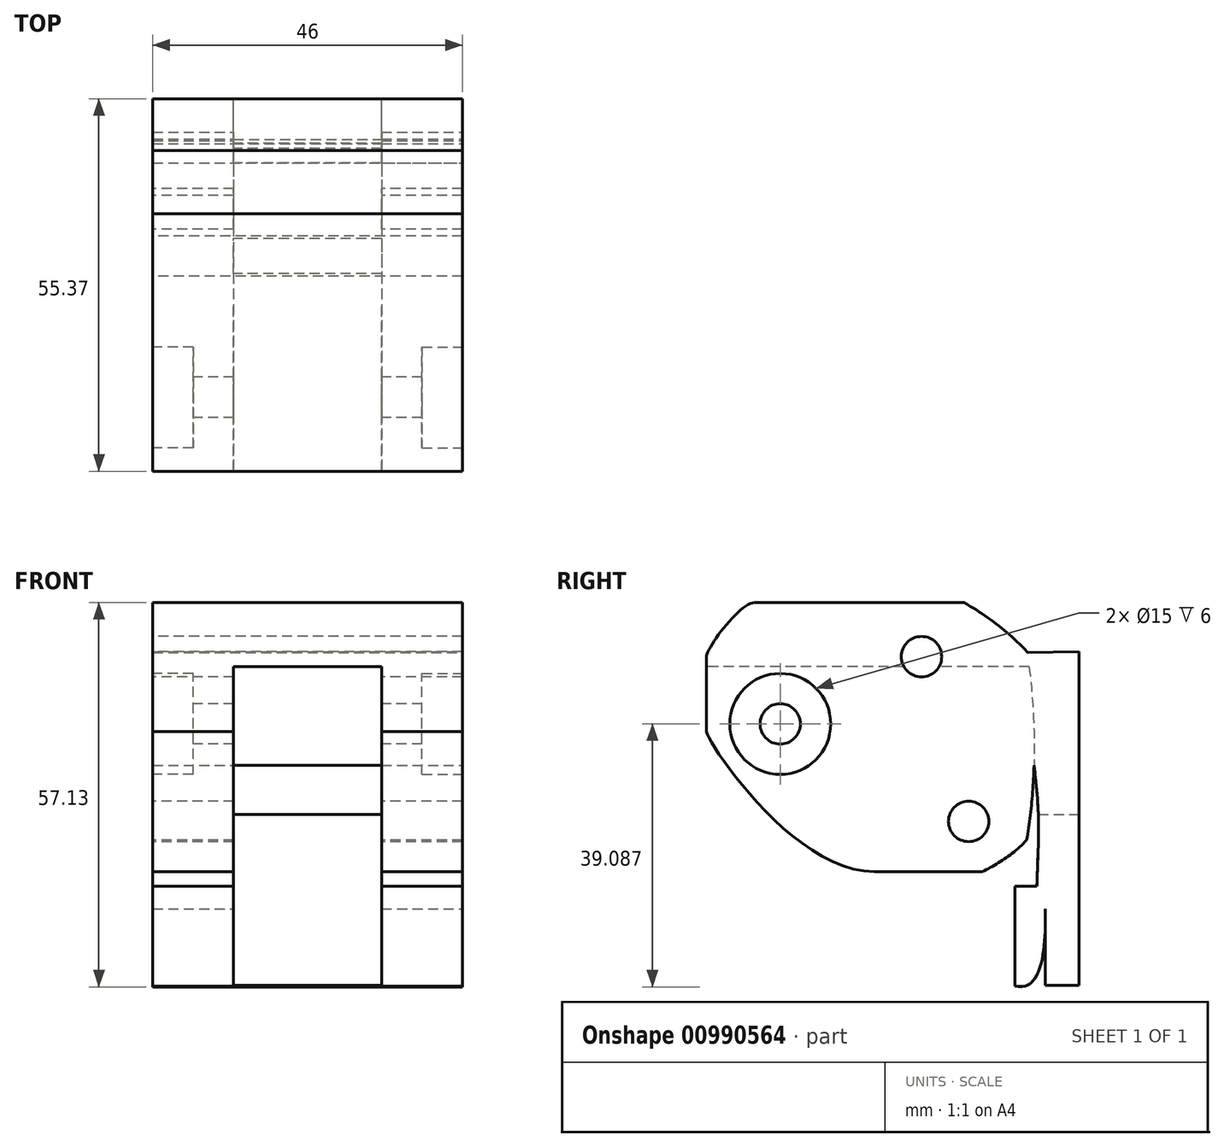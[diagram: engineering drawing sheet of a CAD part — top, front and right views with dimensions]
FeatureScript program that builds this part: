
annotation { "Feature Type Name" : "Feature", "Feature Type Description" : "" }
export const myFeature = defineFeature(function(context is Context, id is Id, definition is map)
    precondition{}
    {
        {
            var Q0;
            Q0=qCreatedBy(makeId("Right.planeOp"),FACE);
            var sketch = newSketch(context, id + "F0", { "sketchPlane" : qUnion([Q0])});
            skLineSegment(sketch, "E0", {"start": v(0, 0) * mm, "end": v(0, -40) * mm});
            skLineSegment(sketch, "E1", {"start": v(0, -40) * mm, "end": v(50, -40) * mm});
            skLineSegment(sketch, "E2", {"start": v(50, -40) * mm, "end": v(50, 0) * mm});
            skLineSegment(sketch, "E3", {"start": v(50, 0) * mm, "end": v(0, 0) * mm});
            skSolve(sketch);
        }
        {
            var Q0;
            Q0=makeQuery(id+"F0.imprint","IMPRINT",FACE,{"disambiguationData":[TD([[makeQuery(id+"F0.imprint","IMPRINT",EDGE,{"derivedFrom":sQuery(id+"F0.wireOp",EDGE,"E0")}),1.0]])]});
            extrude(context, id + "F1", {"entities" : qUnion([Q0]), "depth" : 46 * mm, "offsetDistance" : 25.4 * mm});
        }
        {
            var Q0;
            Q0=makeQuery(id+"F1.opExtrude","SWEPT_FACE",FACE,{"disambiguationData":[OSD([sQuery(id+"F0.wireOp",EDGE,"E0")])]});
            var sketch = newSketch(context, id + "F2", { "sketchPlane" : qUnion([Q0])});
            skLineSegment(sketch, "E4", {"start": v(0, -40) * mm, "end": v(12, -40) * mm});
            skLineSegment(sketch, "E5", {"start": v(12, -40) * mm, "end": v(12, -9.52) * mm});
            skLineSegment(sketch, "E6", {"start": v(12, -9.52) * mm, "end": v(34, -9.52) * mm});
            skLineSegment(sketch, "E7", {"start": v(34, -9.52) * mm, "end": v(34, -40) * mm});
            skLineSegment(sketch, "E8", {"start": v(34, -40) * mm, "end": v(46, -40) * mm});
            skLineSegment(sketch, "E9", {"start": v(12, -40) * mm, "end": v(34, -40) * mm});
            skSolve(sketch);
        }
        {
            var Q0;
            Q0=makeQuery(id+"F2.imprint","IMPRINT",FACE,{"disambiguationData":[TD([[makeQuery(id+"F2.imprint","IMPRINT",EDGE,{"derivedFrom":sQuery(id+"F2.wireOp",EDGE,"E5")}),-1.0]])]});
            extrude(context, id + "F3", {"entities" : qUnion([Q0]), "operationType" : NewBodyOperationType.REMOVE, "oppositeDirection" : true, "depth" : 50 * mm, "offsetDistance" : 25.4 * mm});
        }
        {
            var Q0;
            Q0=makeQuery(id+"F0.imprint","IMPRINT",FACE,{"disambiguationData":[TD([[makeQuery(id+"F0.imprint","IMPRINT",EDGE,{"derivedFrom":sQuery(id+"F0.wireOp",EDGE,"E0")}),1.0]])]});
            var sketch = newSketch(context, id + "F4", { "sketchPlane" : qUnion([Q0])});
            skCircle(sketch, "E10", {"center": v(11, -18.04) * mm, "radius": 3 * mm});
            skLineSegment(sketch, "E11", {"start": v(11, -18.04) * mm, "end": v(11, -40.04) * mm});
            skLineSegment(sketch, "E12", {"start": v(11, -18.04) * mm, "end": v(0, -18.04) * mm});
            skCircle(sketch, "E13", {"center": v(32, -8.04) * mm, "radius": 3 * mm});
            skLineSegment(sketch, "E14", {"start": v(11, -18.04) * mm, "end": v(32, -18.04) * mm});
            skLineSegment(sketch, "E15", {"start": v(32, -18.04) * mm, "end": v(32, -8.04) * mm});
            skCircle(sketch, "E16", {"center": v(39, -32.54) * mm, "radius": 3 * mm});
            skLineSegment(sketch, "E17", {"start": v(39, -32.54) * mm, "end": v(11, -32.54) * mm});
            skLineSegment(sketch, "E18", {"start": v(11, -32.54) * mm, "end": v(11, -18.04) * mm});
            skSolve(sketch);
        }
        {
            var Q0;
            {var subQ0=sQuery(id+"F4.wireOp",EDGE,"E14");var subQ1=sQuery(id+"F4.wireOp",EDGE,"E10");var subQ2=makeQuery(id+"F4.imprint","INTERSECT",VERTEX,{"derivedFrom":[subQ1,subQ0]});Q0=makeQuery(id+"F4.imprint","IMPRINT",FACE,{"disambiguationData":[TD([[makeQuery(id+"F4.imprint","IMPRINT",EDGE,{"disambiguationData":[TD([[subQ2,1.0]])],"derivedFrom":subQ1}),1.0]])]});}
            var Q1;
            {var subQ0=sQuery(id+"F4.wireOp",EDGE,"E12");var subQ1=sQuery(id+"F4.wireOp",EDGE,"E10");var subQ2=makeQuery(id+"F4.imprint","INTERSECT",VERTEX,{"derivedFrom":[subQ1,subQ0]});Q1=makeQuery(id+"F4.imprint","IMPRINT",FACE,{"disambiguationData":[TD([[makeQuery(id+"F4.imprint","IMPRINT",EDGE,{"disambiguationData":[TD([[subQ2,-1.0]])],"derivedFrom":subQ1}),1.0]])]});}
            var Q2;
            {var subQ0=sQuery(id+"F4.wireOp",EDGE,"E14");var subQ1=sQuery(id+"F4.wireOp",EDGE,"E10");var subQ2=makeQuery(id+"F4.imprint","INTERSECT",VERTEX,{"derivedFrom":[subQ1,subQ0]});Q2=makeQuery(id+"F4.imprint","IMPRINT",FACE,{"disambiguationData":[TD([[makeQuery(id+"F4.imprint","IMPRINT",EDGE,{"disambiguationData":[TD([[subQ2,-1.0]])],"derivedFrom":subQ1}),1.0]])]});}
            var Q3;
            Q3=sQuery(id+"F4.wireOp",EDGE,"E10");
            extrude(context, id + "F5", {"entities" : qUnion([Q0, Q1, Q2]), "operationType" : NewBodyOperationType.REMOVE, "surfaceEntities" : qUnion([Q3]), "depth" : 65 * mm, "offsetDistance" : 25.4 * mm});
        }
        {
            var Q0;
            Q0=makeQuery(id+"F4.imprint","IMPRINT",FACE,{"disambiguationData":[TD([[makeQuery(id+"F4.imprint","IMPRINT",EDGE,{"derivedFrom":sQuery(id+"F4.wireOp",EDGE,"E13")}),1.0]])]});
            extrude(context, id + "F6", {"entities" : qUnion([Q0]), "operationType" : NewBodyOperationType.REMOVE, "depth" : 65 * mm, "offsetDistance" : 25.4 * mm});
        }
        {
            var Q0;
            Q0=makeQuery(id+"F4.imprint","IMPRINT",FACE,{"disambiguationData":[TD([[makeQuery(id+"F4.imprint","IMPRINT",EDGE,{"derivedFrom":sQuery(id+"F4.wireOp",EDGE,"E16")}),1.0]])]});
            extrude(context, id + "F7", {"entities" : qUnion([Q0]), "operationType" : NewBodyOperationType.REMOVE, "depth" : 65 * mm, "offsetDistance" : 25.4 * mm});
        }
        {
            var Q0;
            Q0=makeQuery(id+"F0.imprint","IMPRINT",FACE,{"disambiguationData":[TD([[makeQuery(id+"F0.imprint","IMPRINT",EDGE,{"derivedFrom":sQuery(id+"F0.wireOp",EDGE,"E0")}),1.0]])]});
            var sketch = newSketch(context, id + "F8", { "sketchPlane" : qUnion([Q0])});
            skCircle(sketch, "E19", {"center": v(11, -18.04) * mm, "radius": 7.5 * mm});
            skSolve(sketch);
        }
        {
            var Q0;
            Q0=makeQuery(id+"F8.imprint","IMPRINT",FACE,{"disambiguationData":[TD([[makeQuery(id+"F8.imprint","IMPRINT",EDGE,{"derivedFrom":sQuery(id+"F8.wireOp",EDGE,"E19")}),1.0]])]});
            var Q1;
            Q1=sQuery(id+"F8.wireOp",EDGE,"E19");
            extrude(context, id + "F9", {"entities" : qUnion([Q0]), "operationType" : NewBodyOperationType.REMOVE, "surfaceEntities" : qUnion([Q1]), "depth" : 6 * mm, "offsetDistance" : 25.4 * mm});
        }
        {
            var Q0;
            Q0=makeQuery(id+"F1.opExtrude","CAP_FACE",FACE,{"disambiguationData":[OSD([sQuery(id+"F0.wireOp",EDGE,"E0"),sQuery(id+"F0.wireOp",EDGE,"E1"),sQuery(id+"F0.wireOp",EDGE,"E2"),sQuery(id+"F0.wireOp",EDGE,"E3")])],"isStart":false});
            var sketch = newSketch(context, id + "F10", { "sketchPlane" : qUnion([Q0])});
            skCircle(sketch, "E20", {"center": v(11, -18.04) * mm, "radius": 7.5 * mm});
            skSolve(sketch);
        }
        {
            var Q0;
            Q0=makeQuery(id+"F10.imprint","IMPRINT",FACE,{"disambiguationData":[TD([[makeQuery(id+"F10.imprint","IMPRINT",EDGE,{"derivedFrom":sQuery(id+"F10.wireOp",EDGE,"E20")}),1.0]])]});
            extrude(context, id + "F11", {"entities" : qUnion([Q0]), "operationType" : NewBodyOperationType.REMOVE, "oppositeDirection" : true, "depth" : 6 * mm, "offsetDistance" : 25.4 * mm});
        }
        {
            var Q0;
            Q0=makeQuery(id+"F1.opExtrude","CAP_FACE",FACE,{"disambiguationData":[OSD([sQuery(id+"F0.wireOp",EDGE,"E0"),sQuery(id+"F0.wireOp",EDGE,"E1"),sQuery(id+"F0.wireOp",EDGE,"E2"),sQuery(id+"F0.wireOp",EDGE,"E3")])],"isStart":false});
            var sketch = newSketch(context, id + "F12", { "sketchPlane" : qUnion([Q0])});
            skLineSegment(sketch, "E21", {"start": v(0, -19.17) * mm, "end": v(0, -40) * mm});
            skLineSegment(sketch, "E22", {"start": v(0, -40) * mm, "end": v(25, -40) * mm});
            skFitSpline(sketch, "E23", {"points": [v(0, -19.17) * mm, v(25, -40) * mm], "startDerivative": vector(1.52, -6.15) * mm, "endDerivative": vector(36.1, 0) * mm});
            skSolve(sketch);
        }
        {
            var Q0;
            Q0=makeQuery(id+"F12.imprint","IMPRINT",FACE,{"disambiguationData":[TD([[makeQuery(id+"F12.imprint","IMPRINT",EDGE,{"derivedFrom":sQuery(id+"F12.wireOp",EDGE,"E22")}),1.0]])]});
            extrude(context, id + "F13", {"entities" : qUnion([Q0]), "operationType" : NewBodyOperationType.REMOVE, "oppositeDirection" : true, "depth" : 66 * mm, "offsetDistance" : 25.4 * mm});
        }
        {
            var Q0;
            Q0=makeQuery(id+"F1.opExtrude","CAP_FACE",FACE,{"disambiguationData":[OSD([sQuery(id+"F0.wireOp",EDGE,"E0"),sQuery(id+"F0.wireOp",EDGE,"E1"),sQuery(id+"F0.wireOp",EDGE,"E2"),sQuery(id+"F0.wireOp",EDGE,"E3")])],"isStart":false});
            var sketch = newSketch(context, id + "F14", { "sketchPlane" : qUnion([Q0])});
            skLineSegment(sketch, "E24", {"start": v(7.17, 0) * mm, "end": v(0, 0) * mm});
            skLineSegment(sketch, "E25", {"start": v(0, 0) * mm, "end": v(0, -8.13) * mm});
            skFitSpline(sketch, "E26", {"points": [v(7.17, 0) * mm, v(0, -8.13) * mm], "startDerivative": vector(-6.42, 0) * mm, "endDerivative": vector(0, -4.06) * mm});
            skSolve(sketch);
        }
        {
            var Q0;
            Q0=makeQuery(id+"F14.imprint","IMPRINT",FACE,{"disambiguationData":[TD([[makeQuery(id+"F14.imprint","IMPRINT",EDGE,{"derivedFrom":sQuery(id+"F14.wireOp",EDGE,"E24")}),1.0]])]});
            extrude(context, id + "F15", {"entities" : qUnion([Q0]), "operationType" : NewBodyOperationType.REMOVE, "oppositeDirection" : true, "depth" : 100 * mm, "offsetDistance" : 25.4 * mm});
        }
        {
            var Q0;
            Q0=qCreatedBy(makeId("Right.planeOp"),FACE);
            var sketch = newSketch(context, id + "F16", { "sketchPlane" : qUnion([Q0])});
            skFitSpline(sketch, "E27", {"points": [v(38.3, 0) * mm, v(50.02, -10.07) * mm], "startDerivative": vector(13.92, -8.11) * mm, "endDerivative": vector(10.16, -13.26) * mm});
            skFitSpline(sketch, "E28", {"points": [v(50.05, -32.16) * mm, v(40.93, -40.02) * mm], "startDerivative": vector(-7.3, -11.71) * mm, "endDerivative": vector(-10.38, -4.86) * mm});
            skLineSegment(sketch, "E29", {"start": v(38.3, 0) * mm, "end": v(50.02, 0) * mm});
            skLineSegment(sketch, "E30", {"start": v(50.02, 0) * mm, "end": v(50.02, -10.07) * mm});
            skLineSegment(sketch, "E31", {"start": v(50.05, -32.16) * mm, "end": v(50.05, -40.06) * mm});
            skLineSegment(sketch, "E32", {"start": v(50.05, -40.06) * mm, "end": v(40.93, -40.02) * mm});
            skFitSpline(sketch, "E33", {"points": [v(47.68, -7.3) * mm, v(47.62, -35.32) * mm], "startDerivative": vector(4.14, -27.6) * mm, "endDerivative": vector(-4.56, -25.44) * mm});
            skLineSegment(sketch, "E34", {"start": v(47.68, -7.3) * mm, "end": v(50.02, -10.07) * mm});
            skLineSegment(sketch, "E35", {"start": v(50.05, -32.16) * mm, "end": v(47.62, -35.32) * mm});
            skLineSegment(sketch, "E36", {"start": v(50.02, -10.07) * mm, "end": v(50.05, -32.16) * mm});
            skSolve(sketch);
        }
        {
            var Q0;
            Q0 = qSketchRegion(id + "F16", true);
            extrude(context, id + "F17", {"entities" : qUnion([Q0]), "operationType" : NewBodyOperationType.REMOVE, "depth" : 254 * mm, "offsetDistance" : 25.4 * mm});
        }
        {
            var Q0;
            Q0=makeQuery(id+"F1.opExtrude","CAP_FACE",FACE,{"disambiguationData":[OSD([sQuery(id+"F0.wireOp",EDGE,"E0"),sQuery(id+"F0.wireOp",EDGE,"E1"),sQuery(id+"F0.wireOp",EDGE,"E2"),sQuery(id+"F0.wireOp",EDGE,"E3")])],"isStart":false});
            var sketch = newSketch(context, id + "F18", { "sketchPlane" : qUnion([Q0])});
            skLineSegment(sketch, "E37", {"start": v(55.37, -7.33) * mm, "end": v(55.37, -56.91) * mm});
            skLineSegment(sketch, "E38", {"start": v(49.14, -42.18) * mm, "end": v(45.85, -42.18) * mm});
            skLineSegment(sketch, "E39", {"start": v(45.85, -42.18) * mm, "end": v(45.85, -57.04) * mm});
            skLineSegment(sketch, "E40", {"start": v(45.84, -7.44) * mm, "end": v(55.37, -7.33) * mm});
            skFitSpline(sketch, "E41", {"points": [v(45.84, -7.44) * mm, v(49.14, -42.18) * mm], "startDerivative": vector(13.58, -69.76) * mm, "endDerivative": vector(-0.71, -29.2) * mm});
            skLineSegment(sketch, "E42", {"start": v(55.37, -56.91) * mm, "end": v(50.4, -56.91) * mm});
            skLineSegment(sketch, "E43", {"start": v(50.4, -56.91) * mm, "end": v(50.4, -45.54) * mm});
            skFitSpline(sketch, "E44", {"points": [v(50.4, -45.54) * mm, v(45.85, -57.04) * mm], "startDerivative": vector(0, -13.77) * mm, "endDerivative": vector(-13.68, 3.06) * mm});
            skSolve(sketch);
        }
        {
            var Q0;
            {var subQ1=sQuery(id+"F18.wireOp",EDGE,"E37");Q0=makeQuery(id+"F18.imprint","IMPRINT",FACE,{"disambiguationData":[TD([[makeQuery(id+"F18.imprint","IMPRINT",EDGE,{"derivedFrom":subQ1}),-1.0]])]});}
            extrude(context, id + "F19", {"entities" : qUnion([Q0]), "operationType" : NewBodyOperationType.ADD, "oppositeDirection" : true, "depth" : 46 * mm, "offsetDistance" : 25.4 * mm});
        }
        {
            var Q0;
            Q0=makeQuery(id+"F19.opExtrude","SWEPT_FACE",FACE,{"disambiguationData":[OSD([sQuery(id+"F18.wireOp",EDGE,"E37")])]});
            var sketch = newSketch(context, id + "F20", { "sketchPlane" : qUnion([Q0])});
            skLineSegment(sketch, "E45", {"start": v(-34, -56.91) * mm, "end": v(-34, -31.51) * mm});
            skLineSegment(sketch, "E46", {"start": v(-34, -31.51) * mm, "end": v(-12, -31.51) * mm});
            skLineSegment(sketch, "E47", {"start": v(-12, -31.51) * mm, "end": v(-12, -56.91) * mm});
            skLineSegment(sketch, "E48", {"start": v(-34, -56.91) * mm, "end": v(-12, -56.91) * mm});
            skLineSegment(sketch, "E49", {"start": v(-46, -56.91) * mm, "end": v(-34, -56.91) * mm});
            skLineSegment(sketch, "E50", {"start": v(-12, -56.91) * mm, "end": v(0, -56.91) * mm});
            skSolve(sketch);
        }
        {
            var Q0;
            Q0=makeQuery(id+"F20.imprint","IMPRINT",FACE,{"disambiguationData":[TD([[makeQuery(id+"F20.imprint","IMPRINT",EDGE,{"derivedFrom":sQuery(id+"F20.wireOp",EDGE,"E45")}),-1.0]])]});
            extrude(context, id + "F21", {"entities" : qUnion([Q0]), "operationType" : NewBodyOperationType.REMOVE, "oppositeDirection" : true, "depth" : 25.4 * mm, "offsetDistance" : 25.4 * mm});
        }
    });
